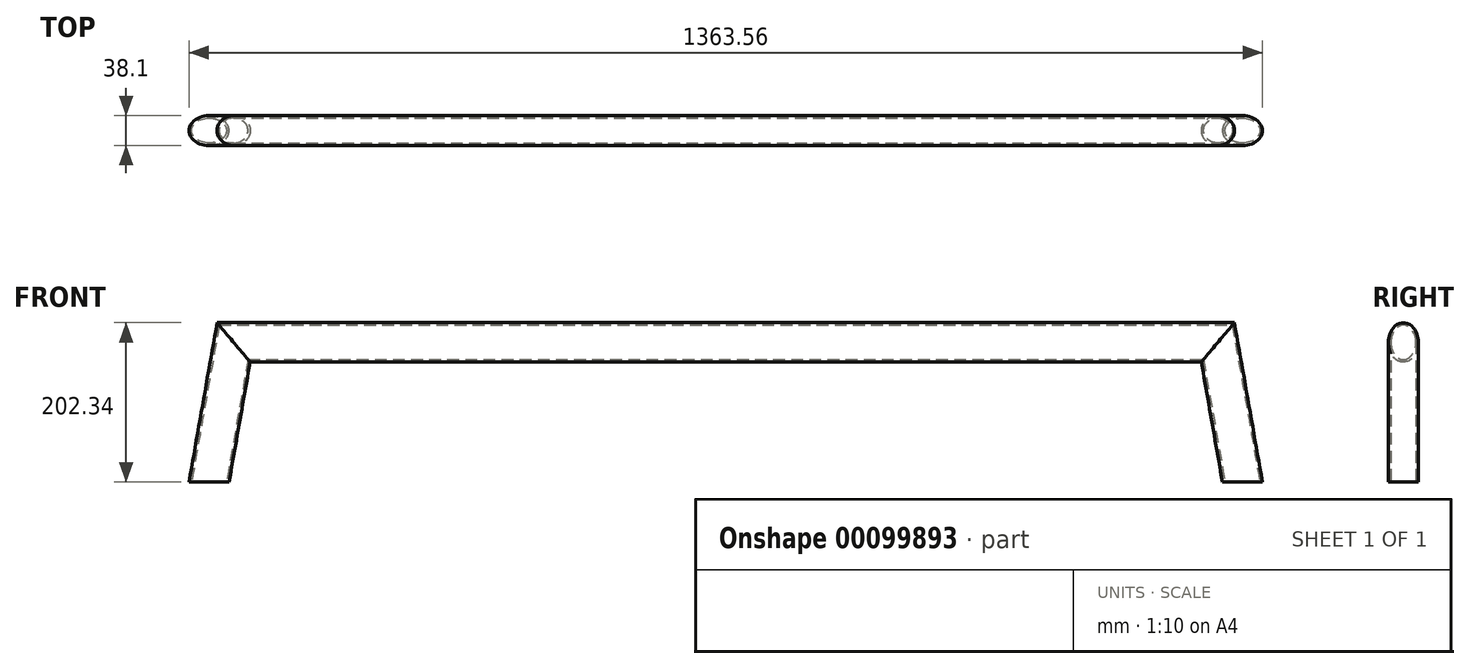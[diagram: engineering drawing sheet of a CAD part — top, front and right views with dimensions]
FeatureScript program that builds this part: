
annotation { "Feature Type Name" : "Feature", "Feature Type Description" : "" }
export const myFeature = defineFeature(function(context is Context, id is Id, definition is map)
    precondition{}
    {
        {
            var Q0;
            Q0=qCreatedBy(makeId("Top.planeOp"),FACE);
            var sketch = newSketch(context, id + "F0", { "sketchPlane" : qUnion([Q0])});
            skEllipse(sketch, "E0", {"center": v(0, 0) * mm, "majorRadius": 25.4 * mm, "minorRadius": 19.05 * mm, "majorAxis": v(1, 0)});
            skEllipse(sketch, "E1", {"center": v(0, 0) * mm, "majorRadius": 22.23 * mm, "minorRadius": 15.88 * mm, "majorAxis": v(1, 0)});
            skSolve(sketch);
        }
        {
            var Q0;
            Q0=qCreatedBy(makeId("Front.planeOp"),FACE);
            var sketch = newSketch(context, id + "F1", { "sketchPlane" : qUnion([Q0])});
            skLineSegment(sketch, "E2", {"start": v(0, 0) * mm, "end": v(35.29, 200.11) * mm});
            skLineSegment(sketch, "E3", {"start": v(35.29, 200.11) * mm, "end": v(1285.51, 200.11) * mm});
            skLineSegment(sketch, "E4", {"start": v(1285.51, 200.11) * mm, "end": v(1320.8, 0) * mm});
            skSolve(sketch);
        }
        {
            var Q0;
            Q0=makeQuery(id+"F0.imprint","IMPRINT",FACE,{"disambiguationData":[TD([[makeQuery(id+"F0.imprint","IMPRINT",EDGE,{"derivedFrom":sQuery(id+"F0.wireOp",EDGE,"E0")}),1.0]])]});
            var Q1;
            Q1=sQuery(id+"F1.wireOp",EDGE,"E2");
            var Q2;
            Q2=sQuery(id+"F1.wireOp",EDGE,"E3");
            var Q3;
            Q3=sQuery(id+"F1.wireOp",EDGE,"E4");
            sweep(context, id + "F2", {"profiles" : qUnion([Q0]), "path" : qUnion([Q1, Q2, Q3])});
        }
        {
            var Q0;
            Q0=qCreatedBy(makeId("Right.planeOp"),FACE);
            var sketch = newSketch(context, id + "F3", { "sketchPlane" : qUnion([Q0])});
            skLineSegment(sketch, "E5.bottom", {"start": v(44.21, 22.8) * mm, "end": v(-44.21, 22.8) * mm});
            skLineSegment(sketch, "E5.top", {"start": v(44.21, -22.8) * mm, "end": v(-44.21, -22.8) * mm});
            skLineSegment(sketch, "E5.left", {"start": v(44.21, 22.8) * mm, "end": v(44.21, -22.8) * mm});
            skLineSegment(sketch, "E5.right", {"start": v(-44.21, 22.8) * mm, "end": v(-44.21, -22.8) * mm});
            skPoint(sketch, "E5.middle", {"position": v(0, 0) * mm});
            skSolve(sketch);
        }
        {
            var Q0;
            Q0 = qSketchRegion(id + "F3", true);
            extrude(context, id + "F4", {"entities" : qUnion([Q0]), "operationType" : NewBodyOperationType.REMOVE, "endBound" : BoundingType.THROUGH_ALL, "depth" : 25.4 * mm, "hasSecondDirection" : true, "secondDirectionBound" : BoundingType.THROUGH_ALL, "secondDirectionOppositeDirection" : true, "secondDirectionDepth" : 25.4 * mm});
        }
    });
